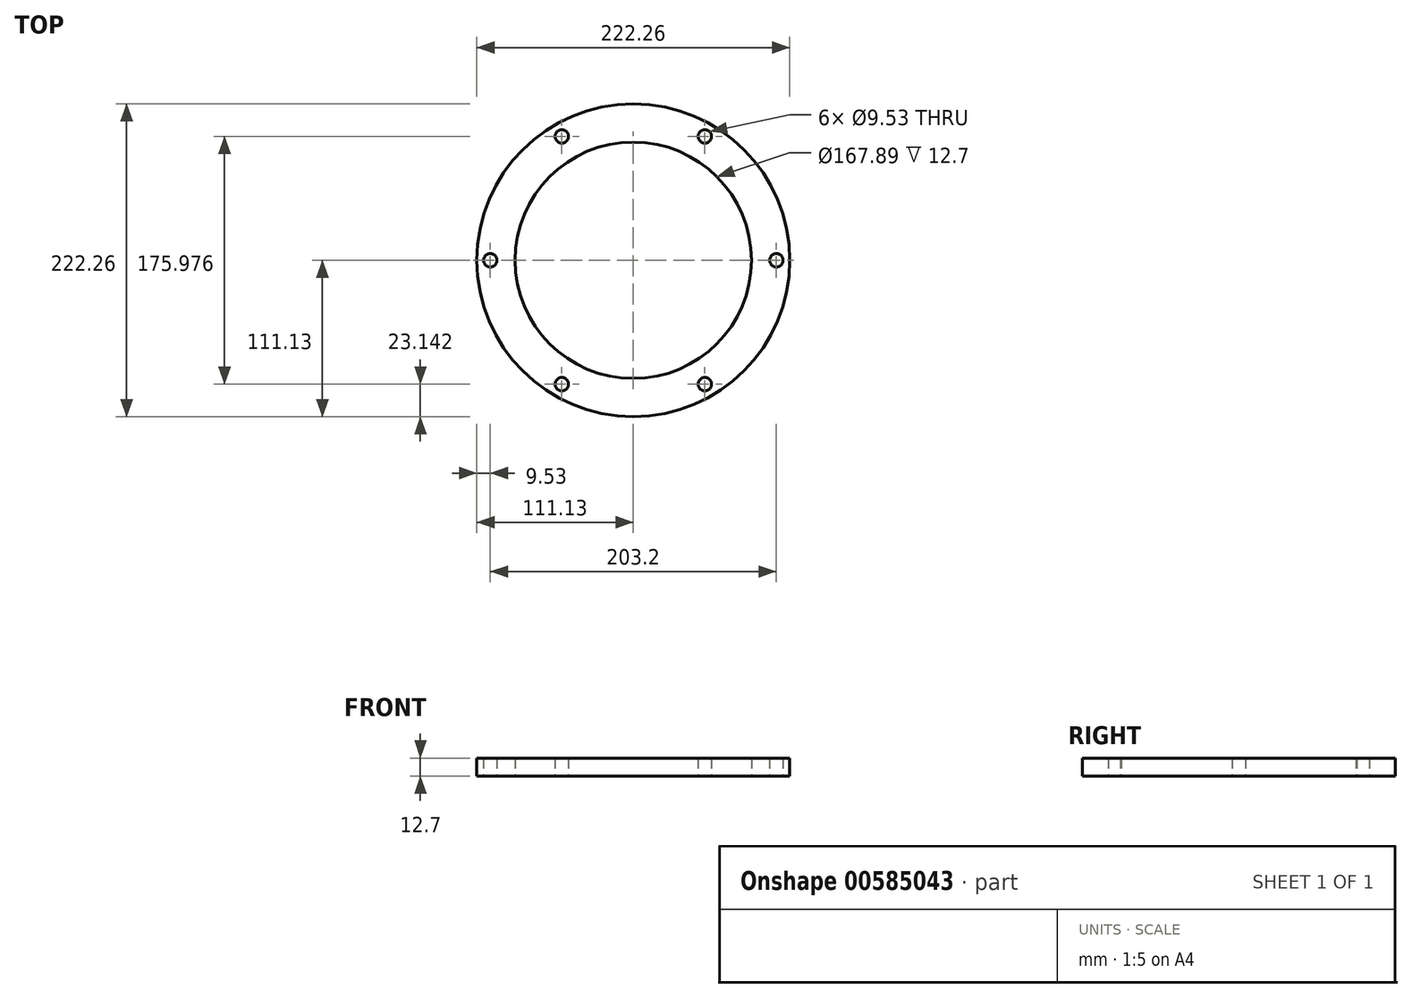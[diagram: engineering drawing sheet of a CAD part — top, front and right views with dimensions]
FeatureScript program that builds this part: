
annotation { "Feature Type Name" : "Feature", "Feature Type Description" : "" }
export const myFeature = defineFeature(function(context is Context, id is Id, definition is map)
    precondition{}
    {
        {
            var Q0;
            Q0=qCreatedBy(makeId("Top.planeOp"),FACE);
            var sketch = newSketch(context, id + "F0", { "sketchPlane" : qUnion([Q0])});
            skCircle(sketch, "E0", {"center": v(0, 0) * mm, "radius": 83.95 * mm});
            skCircle(sketch, "E1", {"center": v(0, 0) * mm, "radius": 111.13 * mm});
            skCircle(sketch, "E2.0", {"center": v(0, 0) * mm, "radius": 101.6 * mm, "construction": true});
            skLineSegment(sketch, "E3", {"start": v(0, 0) * mm, "end": v(0, 101.6) * mm, "construction": true});
            skCircle(sketch, "E4", {"center": v(50.8, 87.99) * mm, "radius": 4.76 * mm});
            skCircle(sketch, "E5.1.0", {"center": v(-50.8, 87.99) * mm, "radius": 4.76 * mm});
            skCircle(sketch, "E5.2.0", {"center": v(-101.6, 0) * mm, "radius": 4.76 * mm});
            skCircle(sketch, "E5.3.0", {"center": v(-50.8, -87.99) * mm, "radius": 4.76 * mm});
            skCircle(sketch, "E5.4.0", {"center": v(50.8, -87.99) * mm, "radius": 4.76 * mm});
            skCircle(sketch, "E5.5.0", {"center": v(101.6, 0) * mm, "radius": 4.76 * mm});
            skSolve(sketch);
        }
        {
            var Q0;
            Q0=makeQuery(id+"F0.imprint","IMPRINT",FACE,{"disambiguationData":[TD([[makeQuery(id+"F0.imprint","IMPRINT",EDGE,{"derivedFrom":sQuery(id+"F0.wireOp",EDGE,"E0")}),-1.0]])]});
            extrude(context, id + "F1", {"entities" : qUnion([Q0]), "depth" : 12.7 * mm, "offsetDistance" : 25.4 * mm});
        }
    });
